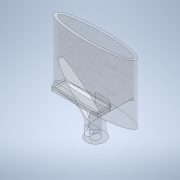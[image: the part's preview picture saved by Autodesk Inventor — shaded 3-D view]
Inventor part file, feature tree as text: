
AUTODESK INVENTOR PART (.ipt)
format: ipt  version: 2020 (Build 240168000, 168)  size: 267,264 bytes
history: native  units: mm
features: sketch x10, extrude x7, plane x3, chamfer x2, thicken_offset x2, loft x1, direct_edit x1, move_body x1
ambient origin geometry x8: Origin, YZ Plane, XZ Plane, XY Plane, X Axis, Y Axis, Z Axis, Center Point
bodies: Solid1 (feature_tree)
feature tree (27):
  sketch  "Sketch1"  dims[d0=20.0mm d1=20.0mm]
  plane  "Work Plane1"
  sketch  "Sketch2"  dims[d2=20.0mm d3=10.0mm]
  plane  "Work Plane2"
  loft  "Loft1"
  extrude  "Extrusion1"  Depth=10.0mm
  extrude  "Extrusion2"  Depth=10.0mm
  extrude  "Extrusion3"  TaperAngle=0.0deg  [1 undecoded]
  extrude  "Extrusion4"  Depth=10.0mm
  chamfer  "Chamfer1"  Distance=30.75mm
  chamfer  "Chamfer2"  Distance=30.0mm
  thicken_offset  "Thicken1"
  thicken_offset  "Thicken2"
  plane  "Work Plane3"
  extrude  "Extrusion5"  Depth=16.0mm TaperAngle=0.0deg
  extrude  "Extrusion6"  Depth=16.0mm TaperAngle=45.0deg
  extrude  "Extrusion7"  Depth=20.0mm
  direct_edit  "Direct Edit1"
  sketch  "Sketch3"  dims[d4=45.0mm d5=10.0mm]
  sketch  "Sketch4"  dims[d6=0.0mm d7=90.0deg d8=0.0mm d9=90.0deg]
  sketch  "Sketch5"  dims[d10=0.0mm d11=90.0deg d12=10.0mm d13=30.75mm d14=0.0mm d15=30.0mm d16=0.0mm]
  sketch  "Sketch6"  dims[d17=25.0mm d18=0.0mm d19=16.0mm d20=0.0mm]
  sketch  "Sketch7"  dims[d21=16.0mm d22=2.0mm d23=45.0deg d24=16.0mm d25=2.0mm d26=45.0deg]
  sketch  "Sketch8"  dims[d27=20.0mm d28=20.0mm]
  sketch  "Sketch9"  dims[d29=20.0mm]
  sketch  "Sketch10"  dims[d30=20.0mm d31=7.75mm d32=50.0mm d33=5.0mm d34=15.0mm d35=0.0mm d36=0.7mm d37=15.0mm d38=0.0mm d39=13.5mm d40=0.0mm d41=0.0mm d42=0.0mm d43=35.0mm]
  move_body  "Move1"
note: 1 required parameter value undecoded (feature->parameter linkage not recoverable at this tier; creation-order binding heuristic only, values carry confidence <= 0.55)
